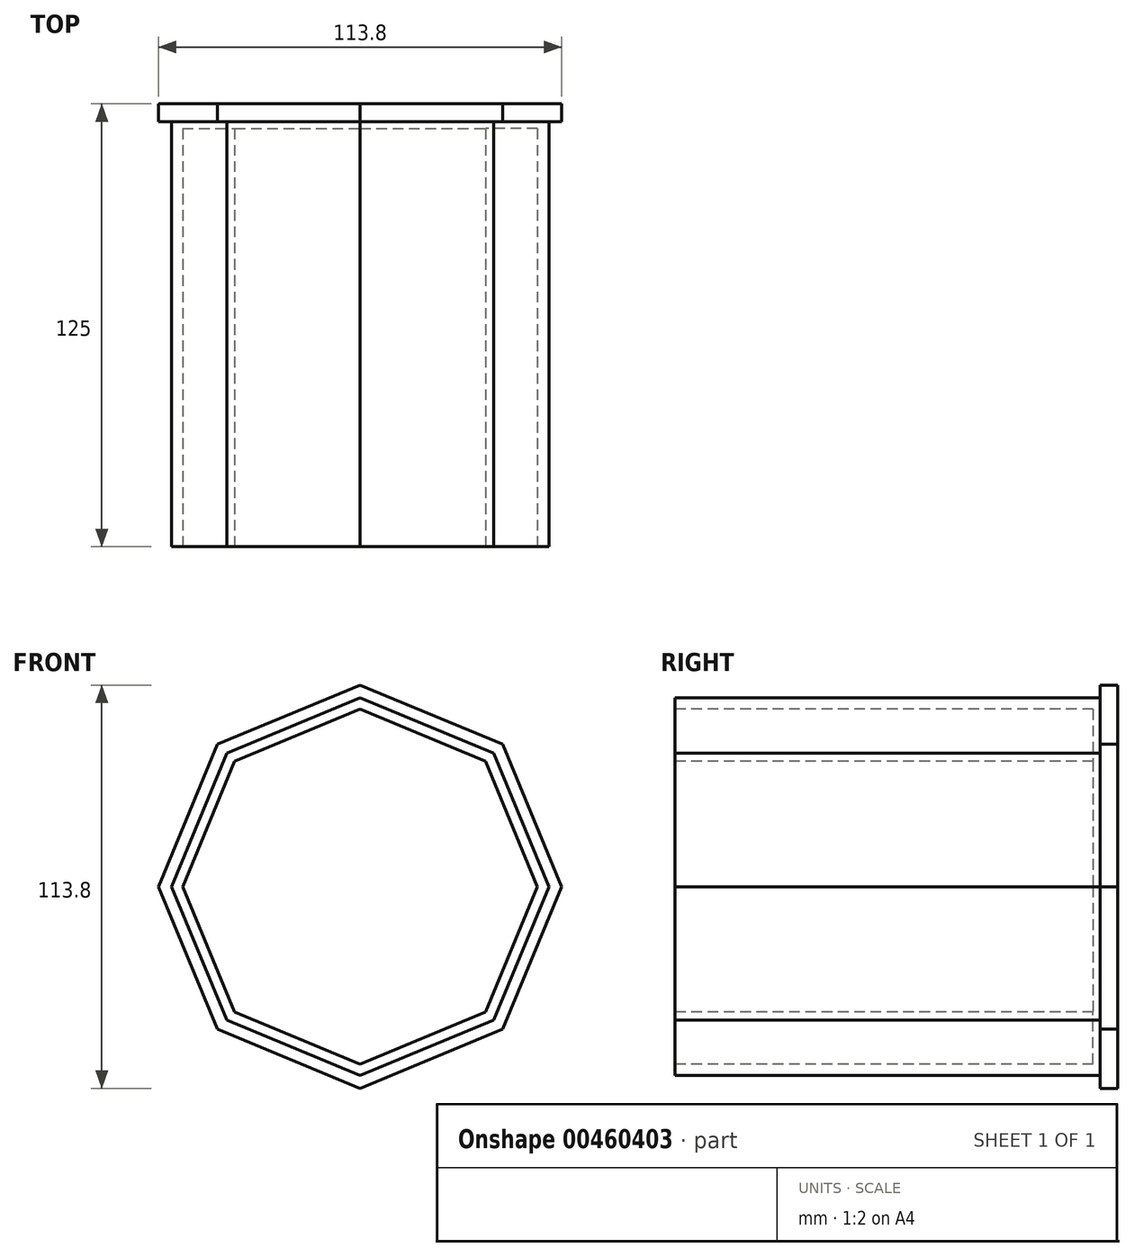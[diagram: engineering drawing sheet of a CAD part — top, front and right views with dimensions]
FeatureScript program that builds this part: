
annotation { "Feature Type Name" : "Feature", "Feature Type Description" : "" }
export const myFeature = defineFeature(function(context is Context, id is Id, definition is map)
    precondition{}
    {
        {
            var Q0;
            Q0=qCreatedBy(makeId("Front.planeOp"),FACE);
            var sketch = newSketch(context, id + "F0", { "sketchPlane" : qUnion([Q0])});
            skLineSegment(sketch, "E0.0", {"start": v(56.9, 0) * mm, "end": v(40.23, -40.23) * mm});
            skLineSegment(sketch, "E0.1", {"start": v(40.23, -40.23) * mm, "end": v(0, -56.9) * mm});
            skLineSegment(sketch, "E0.2", {"start": v(0, -56.9) * mm, "end": v(-40.23, -40.23) * mm});
            skLineSegment(sketch, "E0.3", {"start": v(-40.23, -40.23) * mm, "end": v(-56.9, 0) * mm});
            skLineSegment(sketch, "E0.4", {"start": v(-56.9, 0) * mm, "end": v(-40.23, 40.23) * mm});
            skLineSegment(sketch, "E0.5", {"start": v(-40.23, 40.23) * mm, "end": v(0, 56.9) * mm});
            skLineSegment(sketch, "E0.6", {"start": v(0, 56.9) * mm, "end": v(40.23, 40.23) * mm});
            skLineSegment(sketch, "E0.7", {"start": v(40.23, 40.23) * mm, "end": v(56.9, 0) * mm});
            skSolve(sketch);
        }
        {
            var Q0;
            Q0=qCreatedBy(makeId("Front.planeOp"),FACE);
            cPlane(context, id + "F1", {"entities" : qUnion([Q0]), "cplaneType" : CPlaneType.OFFSET, "offset" : 5 * mm, "width" : 150 * mm, "height" : 150 * mm});
        }
        {
            var Q0;
            Q0 = qSketchRegion(id + "F0", true);
            extrude(context, id + "F2", {"entities" : qUnion([Q0]), "depth" : 5 * mm});
        }
        {
            var Q0;
            Q0=qCreatedBy(id+"F1.planeOp",FACE);
            var sketch = newSketch(context, id + "F3", { "sketchPlane" : qUnion([Q0])});
            skLineSegment(sketch, "E1.0", {"start": v(53.26, 0) * mm, "end": v(37.66, -37.66) * mm});
            skLineSegment(sketch, "E1.1", {"start": v(37.66, -37.66) * mm, "end": v(0, -53.26) * mm});
            skLineSegment(sketch, "E1.2", {"start": v(0, -53.26) * mm, "end": v(-37.66, -37.66) * mm});
            skLineSegment(sketch, "E1.3", {"start": v(-37.66, -37.66) * mm, "end": v(-53.26, 0) * mm});
            skLineSegment(sketch, "E1.4", {"start": v(-53.26, 0) * mm, "end": v(-37.66, 37.66) * mm});
            skLineSegment(sketch, "E1.5", {"start": v(-37.66, 37.66) * mm, "end": v(0, 53.26) * mm});
            skLineSegment(sketch, "E1.6", {"start": v(0, 53.26) * mm, "end": v(37.66, 37.66) * mm});
            skLineSegment(sketch, "E1.7", {"start": v(37.66, 37.66) * mm, "end": v(53.26, 0) * mm});
            skSolve(sketch);
        }
        {
            var Q0;
            Q0=makeQuery(id+"F3.imprint","IMPRINT",FACE,{"disambiguationData":[TD([[makeQuery(id+"F3.imprint","IMPRINT",EDGE,{"derivedFrom":sQuery(id+"F3.wireOp",EDGE,"E1.0")}),-1.0]])]});
            extrude(context, id + "F4", {"entities" : qUnion([Q0]), "operationType" : NewBodyOperationType.ADD, "depth" : 120 * mm});
        }
        {
            var Q0;
            Q0=makeQuery(id+"F4.opExtrude","CAP_FACE",FACE,{"disambiguationData":[OSD([sQuery(id+"F3.wireOp",EDGE,"E1.0"),sQuery(id+"F3.wireOp",EDGE,"E1.1"),sQuery(id+"F3.wireOp",EDGE,"E1.2"),sQuery(id+"F3.wireOp",EDGE,"E1.3"),sQuery(id+"F3.wireOp",EDGE,"E1.4"),sQuery(id+"F3.wireOp",EDGE,"E1.5"),sQuery(id+"F3.wireOp",EDGE,"E1.6"),sQuery(id+"F3.wireOp",EDGE,"E1.7")])],"isStart":false});
            var sketch = newSketch(context, id + "F5", { "sketchPlane" : qUnion([Q0])});
            skLineSegment(sketch, "E2.0", {"start": v(50.07, 0) * mm, "end": v(35.4, -35.4) * mm});
            skLineSegment(sketch, "E2.1", {"start": v(35.4, -35.4) * mm, "end": v(0, -50.07) * mm});
            skLineSegment(sketch, "E2.2", {"start": v(0, -50.07) * mm, "end": v(-35.4, -35.4) * mm});
            skLineSegment(sketch, "E2.3", {"start": v(-35.4, -35.4) * mm, "end": v(-50.07, 0) * mm});
            skLineSegment(sketch, "E2.4", {"start": v(-50.07, 0) * mm, "end": v(-35.4, 35.4) * mm});
            skLineSegment(sketch, "E2.5", {"start": v(-35.4, 35.4) * mm, "end": v(0, 50.07) * mm});
            skLineSegment(sketch, "E2.6", {"start": v(0, 50.07) * mm, "end": v(35.4, 35.4) * mm});
            skLineSegment(sketch, "E2.7", {"start": v(35.4, 35.4) * mm, "end": v(50.07, 0) * mm});
            skSolve(sketch);
        }
        {
            var Q0;
            Q0=makeQuery(id+"F5.imprint","IMPRINT",FACE,{"disambiguationData":[TD([[makeQuery(id+"F5.imprint","IMPRINT",EDGE,{"derivedFrom":sQuery(id+"F5.wireOp",EDGE,"E2.0")}),-1.0]])]});
            extrude(context, id + "F6", {"entities" : qUnion([Q0]), "operationType" : NewBodyOperationType.REMOVE, "oppositeDirection" : true, "depth" : 118 * mm});
        }
    });
